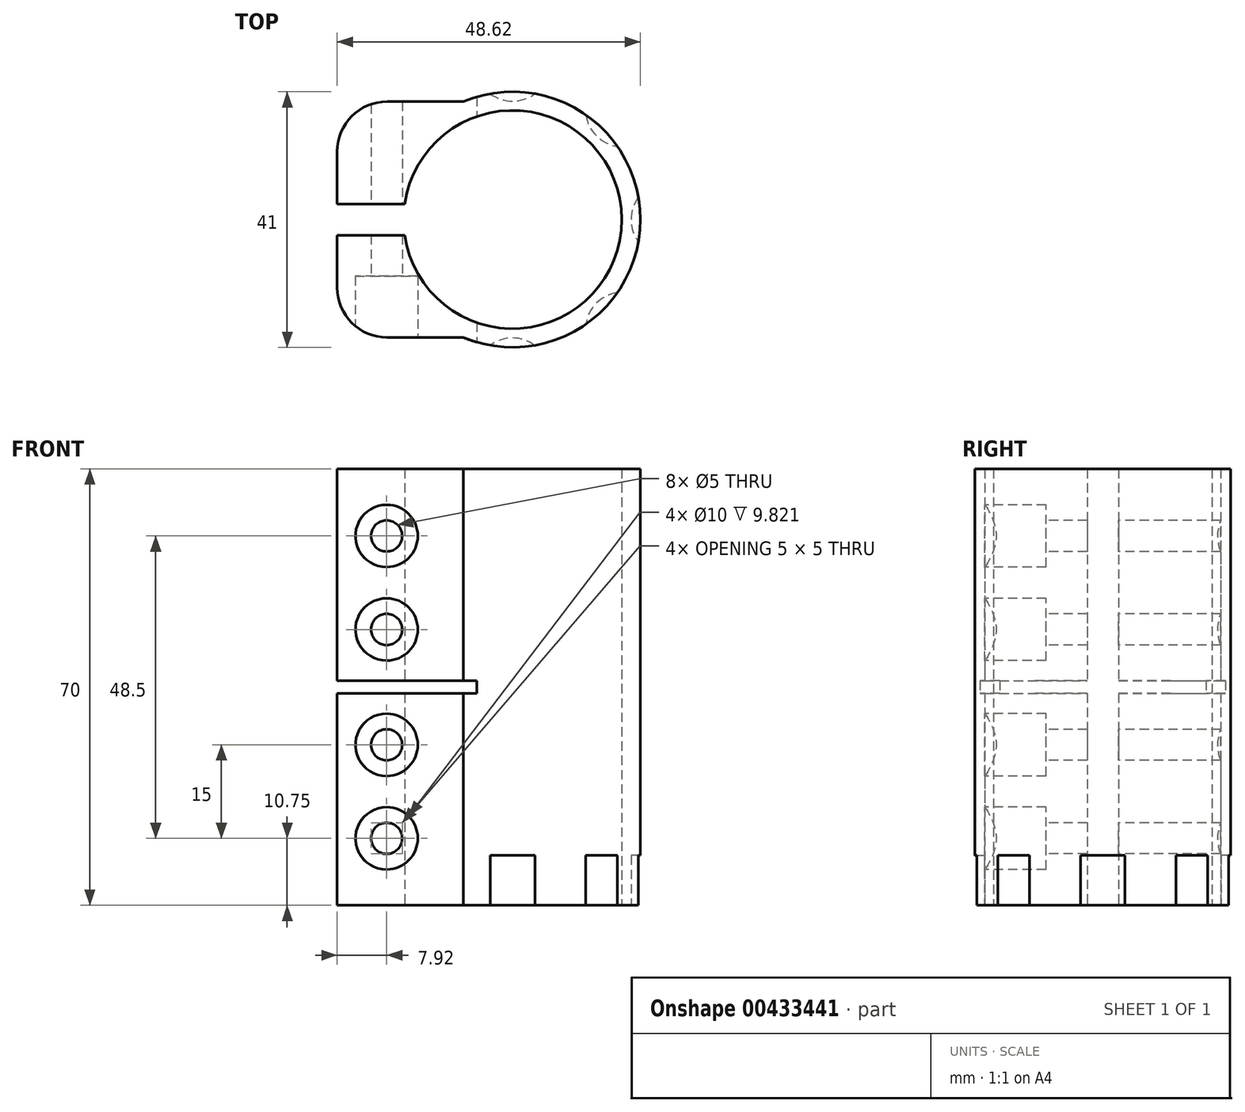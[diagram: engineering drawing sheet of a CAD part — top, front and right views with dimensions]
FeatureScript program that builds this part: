
annotation { "Feature Type Name" : "Feature", "Feature Type Description" : "" }
export const myFeature = defineFeature(function(context is Context, id is Id, definition is map)
    precondition{}
    {
        {
            var Q0;
            Q0=qCreatedBy(makeId("Top.planeOp"),FACE);
            var sketch = newSketch(context, id + "F0", { "sketchPlane" : qUnion([Q0])});
            skArc(sketch, "E0", {"start": v(-17.32, -2.5) * mm, "mid": v(17.5, 0) * mm, "end": v(-17.32, 2.5) * mm});
            skLineSegment(sketch, "E1", {"start": v(-7.92, 18.9) * mm, "end": v(-20.12, 18.9) * mm});
            skLineSegment(sketch, "E2", {"start": v(-28.12, 10.9) * mm, "end": v(-28.12, 2.5) * mm});
            skLineSegment(sketch, "E3", {"start": v(-28.12, 2.5) * mm, "end": v(-17.32, 2.5) * mm});
            skPoint(sketch, "E4.visualSharp", {"position": v(-28.12, 18.9) * mm});
            skArc(sketch, "E4.filletArc", {"start": v(-20.12, 18.9) * mm, "mid": v(-25.78, 16.57) * mm, "end": v(-28.12, 10.9) * mm});
            skLineSegment(sketch, "E5.MirrorCS", {"start": v(-7.92, -18.9) * mm, "end": v(-20.12, -18.9) * mm});
            skArc(sketch, "E6.MirrorCS", {"start": v(-20.12, -18.9) * mm, "mid": v(-25.78, -16.57) * mm, "end": v(-28.12, -10.9) * mm});
            skLineSegment(sketch, "E7.MirrorCS", {"start": v(-28.12, -2.5) * mm, "end": v(-17.32, -2.5) * mm});
            skLineSegment(sketch, "E8.MirrorCS", {"start": v(-28.12, -10.9) * mm, "end": v(-28.12, -2.5) * mm});
            skArc(sketch, "E9.trimOffspring", {"start": v(-7.92, -18.9) * mm, "mid": v(20.5, 0) * mm, "end": v(-7.92, 18.9) * mm});
            skSolve(sketch);
        }
        {
            var Q0;
            Q0=qSketchRegion(id+"F0",true);
            extrude(context, id + "F1", {"entities" : qUnion([Q0]), "endBound" : BoundingType.SYMMETRIC, "depth" : 70 * mm});
        }
        {
            var Q0;
            Q0=makeQuery(id+"F1.opExtrude","SWEPT_FACE",FACE,{"disambiguationData":[OSD([sQuery(id+"F0.wireOp",EDGE,"E5.MirrorCS")])]});
            var sketch = newSketch(context, id + "F2", { "sketchPlane" : qUnion([Q0])});
            skPoint(sketch, "E10", {"position": v(-20.2, -24.25) * mm});
            skPoint(sketch, "E11", {"position": v(-20.2, -9.25) * mm});
            skPoint(sketch, "E12", {"position": v(-20.2, 9.25) * mm});
            skPoint(sketch, "E13", {"position": v(-20.2, 24.25) * mm});
            skSolve(sketch);
        }
        {
            var Q0;
            Q0=sQuery(id+"F2.wireOp",VERTEX,"E10");
            var Q1;
            Q1=sQuery(id+"F2.wireOp",VERTEX,"E11");
            var Q2;
            Q2=sQuery(id+"F2.wireOp",VERTEX,"E12");
            var Q3;
            Q3=sQuery(id+"F2.wireOp",VERTEX,"E13");
            var Q4;
            Q4=makeQuery(id+"F1.opExtrude","SWEPT_BODY",BODY,{"disambiguationData":[OSD([sQuery(id+"F0.wireOp",EDGE,"E0"),sQuery(id+"F0.wireOp",EDGE,"E1"),sQuery(id+"F0.wireOp",EDGE,"E2"),sQuery(id+"F0.wireOp",EDGE,"E3"),sQuery(id+"F0.wireOp",EDGE,"E4.filletArc"),sQuery(id+"F0.wireOp",EDGE,"E5.MirrorCS"),sQuery(id+"F0.wireOp",EDGE,"E6.MirrorCS"),sQuery(id+"F0.wireOp",EDGE,"E7.MirrorCS"),sQuery(id+"F0.wireOp",EDGE,"E8.MirrorCS"),sQuery(id+"F0.wireOp",EDGE,"E9.trimOffspring")])]});
            hole(context, id + "F3", {"style" : HoleStyle.C_BORE, "endStyle" : HoleEndStyle.THROUGH, "holeDiameter" : 5 * mm, "cBoreDiameter" : 10 * mm, "cBoreDepth" : 8 * mm, "isTappedThrough" : true, "tappedDepth" : 12 * mm, "tapClearance" : 3, "locations" : qUnion([Q0, Q1, Q2, Q3]), "scope" : qUnion([Q4])});
        }
        {
            var Q0;
            Q0=qCreatedBy(makeId("Front.planeOp"),FACE);
            var sketch = newSketch(context, id + "F4", { "sketchPlane" : qUnion([Q0])});
            skLineSegment(sketch, "E14.bottom", {"start": v(-28.12, 1) * mm, "end": v(-5.72, 1) * mm});
            skLineSegment(sketch, "E14.top", {"start": v(-28.12, -1) * mm, "end": v(-5.72, -1) * mm});
            skLineSegment(sketch, "E14.left", {"start": v(-28.12, 1) * mm, "end": v(-28.12, -1) * mm});
            skLineSegment(sketch, "E14.right", {"start": v(-5.72, 1) * mm, "end": v(-5.72, -1) * mm});
            skSolve(sketch);
        }
        {
            var Q0;
            Q0=qSketchRegion(id+"F4",true);
            extrude(context, id + "F5", {"entities" : qUnion([Q0]), "operationType" : NewBodyOperationType.REMOVE, "endBound" : BoundingType.SYMMETRIC, "oppositeDirection" : true, "depth" : 50 * mm});
        }
        {
            var Q0;
            Q0=makeQuery(id+"F1.opExtrude","CAP_FACE",FACE,{"disambiguationData":[OSD([sQuery(id+"F0.wireOp",EDGE,"E0"),sQuery(id+"F0.wireOp",EDGE,"E1"),sQuery(id+"F0.wireOp",EDGE,"E2"),sQuery(id+"F0.wireOp",EDGE,"E3"),sQuery(id+"F0.wireOp",EDGE,"E4.filletArc"),sQuery(id+"F0.wireOp",EDGE,"E5.MirrorCS"),sQuery(id+"F0.wireOp",EDGE,"E6.MirrorCS"),sQuery(id+"F0.wireOp",EDGE,"E7.MirrorCS"),sQuery(id+"F0.wireOp",EDGE,"E8.MirrorCS"),sQuery(id+"F0.wireOp",EDGE,"E9.trimOffspring")])],"isStart":true});
            var sketch = newSketch(context, id + "F6", { "sketchPlane" : qUnion([Q0])});
            skCircle(sketch, "E15", {"center": v(0, 25) * mm, "radius": 6 * mm});
            skCircle(sketch, "E16.1.0", {"center": v(17.68, 17.68) * mm, "radius": 6 * mm});
            skCircle(sketch, "E16.2.0", {"center": v(25, 0) * mm, "radius": 6 * mm});
            skCircle(sketch, "E16.3.0", {"center": v(17.68, -17.68) * mm, "radius": 6 * mm});
            skCircle(sketch, "E16.4.0", {"center": v(0, -25) * mm, "radius": 6 * mm});
            skPoint(sketch, "E16.center", {"position": v(0, 0) * mm});
            skLineSegment(sketch, "E16.anchor1", {"start": v(0, 0) * mm, "end": v(0, 25) * mm, "construction": true});
            skLineSegment(sketch, "E16.anchor2", {"start": v(0, 0) * mm, "end": v(0, -25) * mm, "construction": true});
            skSolve(sketch);
        }
        {
            var Q0;
            Q0=qSketchRegion(id+"F6",true);
            extrude(context, id + "F7", {"entities" : qUnion([Q0]), "operationType" : NewBodyOperationType.REMOVE, "oppositeDirection" : true, "depth" : 8 * mm});
        }
    });
